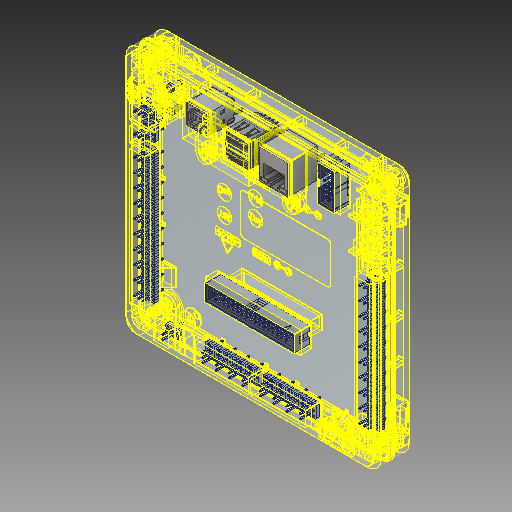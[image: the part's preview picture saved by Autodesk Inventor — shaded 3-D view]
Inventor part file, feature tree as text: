
AUTODESK INVENTOR PART (.ipt)
format: ipt  version: 2017 (Build 210142000, 142)  size: 32,417,792 bytes
history: mixed  units: in
note: dims shown in document units (in); Inventor stores cm internally (conversion verified against a paired STEP export)
features: chamfer x9, imported_body x6, other x2
ambient origin geometry x8: Origin, YZ Plane, XZ Plane, XY Plane, X Axis, Y Axis, Z Axis, Center Point
bodies: Solid1 (imported_parasolid), Solid2 (imported_parasolid), Solid3 (imported_parasolid), Solid4 (imported_parasolid), Solid5 (imported_parasolid), Solid6 (imported_parasolid), Solid7 (imported_parasolid), Solid8 (imported_parasolid), Solid9 (imported_parasolid), Solid10 (imported_parasolid), Solid11 (imported_parasolid), Solid12 (imported_parasolid), Solid13 (imported_parasolid), Solid14 (imported_parasolid)
feature tree (17):
  imported_body  "Imported1"
  imported_body  "Imported2"
  imported_body  "Imported6"
  imported_body  "Imported7"
  imported_body  "Imported15"
  chamfer  "Chamfer1"  [1 undecoded]
  chamfer  "Chamfer2"  [1 undecoded]
  chamfer  "Chamfer3"  [1 undecoded]
  chamfer  "Chamfer4"  [1 undecoded]
  chamfer  "Chamfer5"  [1 undecoded]
  chamfer  "Chamfer6"  [1 undecoded]
  chamfer  "Chamfer7"  [1 undecoded]
  chamfer  "Chamfer8"  [1 undecoded]
  chamfer  "Chamfer9"  [1 undecoded]
  other  "Composite1"
  other  "Srf1"
  imported_body  NMx_Import_Brep_tag  [imported B-rep: ~113 faces, bbox_mm=[129.281002, 132.48844, 14.46]]
note: 9 required parameter values undecoded (feature->parameter linkage not recoverable at this tier; creation-order binding heuristic only, values carry confidence <= 0.55)
